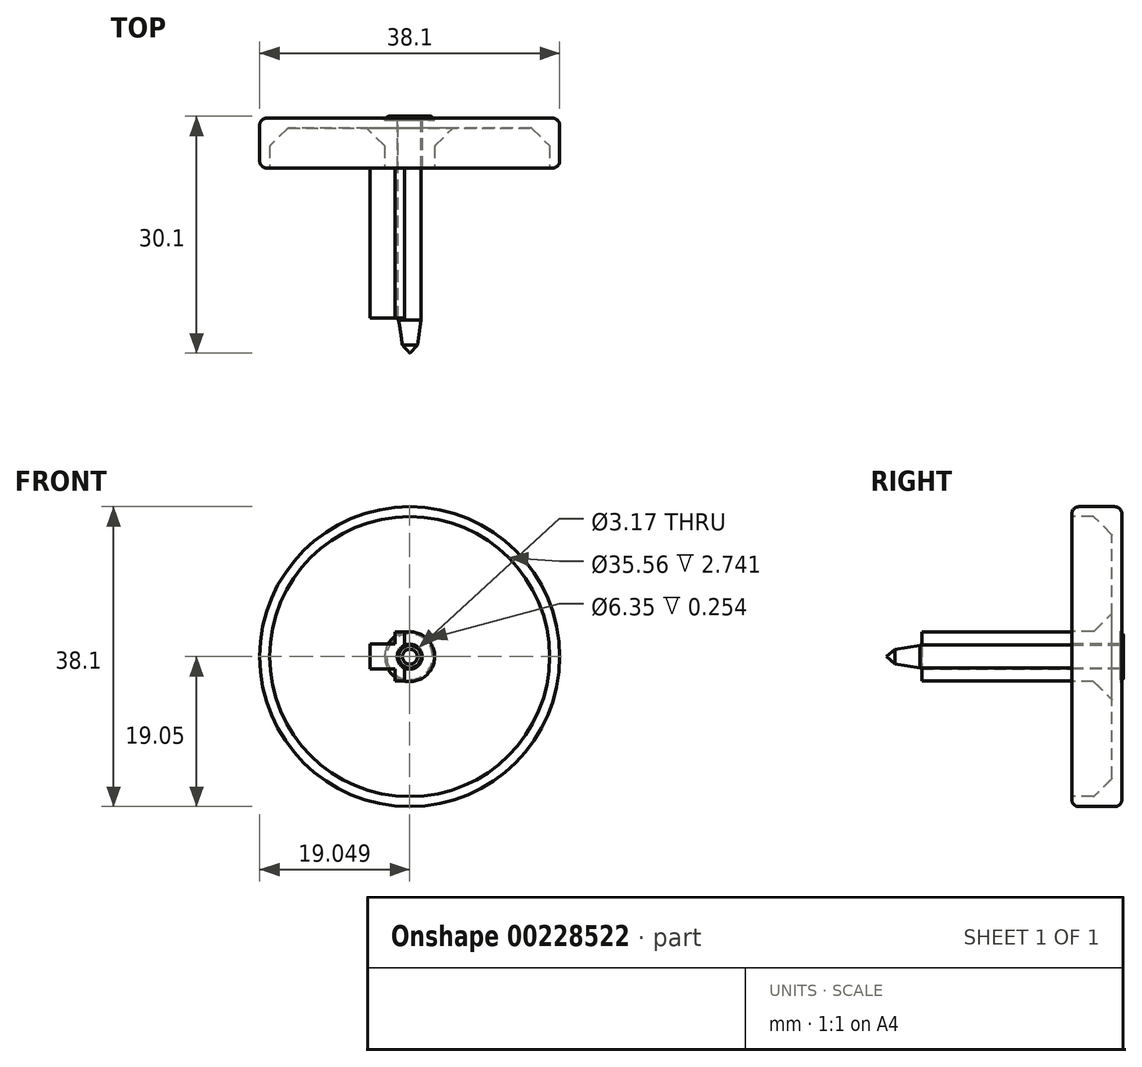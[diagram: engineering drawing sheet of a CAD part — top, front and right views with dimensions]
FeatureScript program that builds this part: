
annotation { "Feature Type Name" : "Feature", "Feature Type Description" : "" }
export const myFeature = defineFeature(function(context is Context, id is Id, definition is map)
    precondition{}
    {
        {
            var Q0;
            Q0=qCreatedBy(makeId("Front.planeOp"),FACE);
            var sketch = newSketch(context, id + "F0", { "sketchPlane" : qUnion([Q0])});
            skCircle(sketch, "E0", {"center": v(0.63, 0) * mm, "radius": 19.05 * mm});
            skSolve(sketch);
        }
        {
            var Q0;
            Q0=makeQuery(id+"F0.imprint","IMPRINT",FACE,{"disambiguationData":[TD([[makeQuery(id+"F0.imprint","IMPRINT",EDGE,{"derivedFrom":sQuery(id+"F0.wireOp",EDGE,"E0")}),1.0]])]});
            extrude(context, id + "F1", {"entities" : qUnion([Q0]), "depth" : 6.35 * mm});
        }
        {
            var Q0;
            Q0=makeQuery(id+"F1.opExtrude","CAP_FACE",FACE,{"disambiguationData":[OSD([sQuery(id+"F0.wireOp",EDGE,"E0")])],"isStart":false});
            var sketch = newSketch(context, id + "F2", { "sketchPlane" : qUnion([Q0])});
            skCircle(sketch, "E1", {"center": v(0.63, 0) * mm, "radius": 17.78 * mm});
            skCircle(sketch, "E2", {"center": v(0.63, 0) * mm, "radius": 3.18 * mm});
            skSolve(sketch);
        }
        {
            var Q0;
            Q0=makeQuery(id+"F2.imprint","IMPRINT",FACE,{"disambiguationData":[TD([[makeQuery(id+"F2.imprint","IMPRINT",EDGE,{"derivedFrom":sQuery(id+"F2.wireOp",EDGE,"E1")}),1.0]])]});
            extrude(context, id + "F3", {"entities" : qUnion([Q0]), "operationType" : NewBodyOperationType.REMOVE, "oppositeDirection" : true, "depth" : 5.08 * mm});
        }
        {
            var Q0;
            Q0=makeQuery(id+"F3.boolean.opBoolean","SPLIT",FACE,{"disambiguationData":[TD([makeQuery(id+"F3.opExtrude","SWEPT_FACE",FACE,{"disambiguationData":[OSD([sQuery(id+"F2.wireOp",EDGE,"E2")])]})])],"derivedFrom":makeQuery(id+"F1.opExtrude","CAP_FACE",FACE,{"disambiguationData":[OSD([sQuery(id+"F0.wireOp",EDGE,"E0")])],"isStart":false})});
            var sketch = newSketch(context, id + "F4", { "sketchPlane" : qUnion([Q0])});
            skCircle(sketch, "E3", {"center": v(0.63, 0) * mm, "radius": 1.59 * mm});
            skSolve(sketch);
        }
        {
            var Q0;
            Q0=qSketchRegion(id+"F4",true);
            var Q1;
            Q1=makeQuery(id+"F1.opExtrude","CAP_FACE",FACE,{"disambiguationData":[OSD([sQuery(id+"F0.wireOp",EDGE,"E0")])],"isStart":true});
            extrude(context, id + "F5", {"entities" : qUnion([Q0]), "operationType" : NewBodyOperationType.REMOVE, "endBound" : BoundingType.UP_TO_SURFACE, "oppositeDirection" : true, "endBoundEntityFace" : qUnion([Q1]), "depth" : 25.4 * mm});
        }
        {
            var Q0;
            Q0=makeQuery(id+"F1.opExtrude","CAP_FACE",FACE,{"disambiguationData":[OSD([sQuery(id+"F0.wireOp",EDGE,"E0")])],"isStart":true});
            var sketch = newSketch(context, id + "F6", { "sketchPlane" : qUnion([Q0])});
            skCircle(sketch, "E4", {"center": v(-0.63, 0) * mm, "radius": 3.18 * mm});
            skSolve(sketch);
        }
        {
            var Q0;
            Q0=qSketchRegion(id+"F6",true);
            extrude(context, id + "F7", {"entities" : qUnion([Q0]), "operationType" : NewBodyOperationType.REMOVE, "oppositeDirection" : true, "depth" : 0.25 * mm});
        }
        {
            var Q0;
            Q0=makeQuery(id+"F7.boolean.opBoolean","COPY",FACE,{"derivedFrom":makeQuery(id+"F7.opExtrude","CAP_FACE",FACE,{"disambiguationData":[OSD([sQuery(id+"F6.wireOp",EDGE,"E4")])],"isStart":false})});
            var sketch = newSketch(context, id + "F8", { "sketchPlane" : qUnion([Q0])});
            skCircle(sketch, "E5", {"center": v(-0.63, 0) * mm, "radius": 1.46 * mm});
            skSolve(sketch);
        }
        {
            var Q0;
            Q0=qSketchRegion(id+"F8",true);
            extrude(context, id + "F9", {"entities" : qUnion([Q0]), "oppositeDirection" : true, "depth" : 25.4 * mm});
        }
        {
            var Q0;
            Q0=qCreatedBy(makeId("Top.planeOp"),FACE);
            var sketch = newSketch(context, id + "F10", { "sketchPlane" : qUnion([Q0])});
            skLineSegment(sketch, "E6", {"start": v(0.66, -25.65) * mm, "end": v(0.66, -29.87) * mm});
            skLineSegment(sketch, "E7", {"start": v(0.66, -29.87) * mm, "end": v(1.6, -28.83) * mm});
            skLineSegment(sketch, "E8", {"start": v(1.6, -28.83) * mm, "end": v(2.09, -25.65) * mm});
            skLineSegment(sketch, "E9", {"start": v(2.09, -25.65) * mm, "end": v(0.66, -25.65) * mm});
            skSolve(sketch);
        }
        {
            var Q0;
            Q0=makeQuery(id+"F10.imprint","IMPRINT",FACE,{"disambiguationData":[TD([[makeQuery(id+"F10.imprint","IMPRINT",EDGE,{"derivedFrom":sQuery(id+"F10.wireOp",EDGE,"E6")}),1.0]])]});
            var Q1;
            Q1=sQuery(id+"F10.wireOp",EDGE,"E6");
            revolve(context, id + "F11", {"operationType" : NewBodyOperationType.ADD, "entities" : qUnion([Q0]), "axis" : qUnion([Q1]), "revolveType" : RevolveType.FULL});
        }
        {
            var Q0;
            Q0=makeQuery(id+"F9.opExtrude","CAP_FACE",FACE,{"disambiguationData":[OSD([sQuery(id+"F8.wireOp",EDGE,"E5")])],"isStart":true});
            var sketch = newSketch(context, id + "F12", { "sketchPlane" : qUnion([Q0])});
            skCircle(sketch, "E10", {"center": v(-0.63, 0) * mm, "radius": 2.92 * mm});
            skSolve(sketch);
        }
        {
            var Q0;
            Q0=qSketchRegion(id+"F12",true);
            extrude(context, id + "F13", {"entities" : qUnion([Q0]), "depth" : 0.48 * mm});
        }
        {
            var Q0;
            Q0=makeQuery(id+"F13.opExtrude","CAP_EDGE",EDGE,{"disambiguationData":[OSD([sQuery(id+"F12.wireOp",EDGE,"E10")])],"isStart":false});
            var Q1;
            Q1=makeQuery(id+"F7.boolean.opBoolean","COPY",EDGE,{"derivedFrom":makeQuery(id+"F7.opExtrude","CAP_EDGE",EDGE,{"disambiguationData":[OSD([sQuery(id+"F6.wireOp",EDGE,"E4")])],"isStart":true})});
            fillet(context, id + "F14", {"entities" : qUnion([Q0, Q1]), "radius" : 0.25 * mm, "tangentPropagation" : true, "allowEdgeOverflow" : false});
        }
        {
            var Q0;
            Q0=makeQuery(id+"F1.opExtrude","CAP_EDGE",EDGE,{"disambiguationData":[OSD([sQuery(id+"F0.wireOp",EDGE,"E0")])],"isStart":true});
            var Q1;
            Q1=makeQuery(id+"F1.opExtrude","CAP_EDGE",EDGE,{"disambiguationData":[OSD([sQuery(id+"F0.wireOp",EDGE,"E0")])],"isStart":false});
            fillet(context, id + "F15", {"entities" : qUnion([Q0, Q1]), "radius" : 0.89 * mm, "tangentPropagation" : true, "allowEdgeOverflow" : false});
        }
        {
            var Q0;
            Q0=makeQuery(id+"F3.boolean.opBoolean","COPY",FACE,{"derivedFrom":makeQuery(id+"F3.opExtrude","CAP_FACE",FACE,{"disambiguationData":[OSD([sQuery(id+"F2.wireOp",EDGE,"E1"),sQuery(id+"F2.wireOp",EDGE,"E2")])],"isStart":false})});
            chamfer(context, id + "F16", {"entities" : qUnion([Q0]), "width" : 2.3 * mm, "tangentPropagation" : true});
        }
        {
            var Q0;
            {var subQ0=sQuery(id+"F2.wireOp",EDGE,"E1");Q0=makeQuery(id+"F16.opChamfer","BLEND_EDGE",EDGE,{"blendedFrom":[makeQuery(id+"F3.boolean.opBoolean","COPY",EDGE,{"derivedFrom":makeQuery(id+"F3.opExtrude","CAP_EDGE",EDGE,{"disambiguationData":[OSD([subQ0])],"isStart":false})}),makeQuery(id+"F3.boolean.opBoolean","COPY",FACE,{"derivedFrom":makeQuery(id+"F3.opExtrude","CAP_FACE",FACE,{"disambiguationData":[OSD([subQ0,sQuery(id+"F2.wireOp",EDGE,"E2")])],"isStart":false})})],"blendedInto":[makeQuery(id+"F3.boolean.opBoolean","COPY",FACE,{"derivedFrom":makeQuery(id+"F3.opExtrude","CAP_FACE",FACE,{"disambiguationData":[OSD([subQ0,sQuery(id+"F2.wireOp",EDGE,"E2")])],"isStart":false})})]});}
            var Q1;
            {var subQ0=sQuery(id+"F2.wireOp",EDGE,"E2");Q1=makeQuery(id+"F16.opChamfer","BLEND_EDGE",EDGE,{"blendedFrom":[makeQuery(id+"F3.boolean.opBoolean","COPY",EDGE,{"derivedFrom":makeQuery(id+"F3.opExtrude","CAP_EDGE",EDGE,{"disambiguationData":[OSD([subQ0])],"isStart":false})}),makeQuery(id+"F3.boolean.opBoolean","COPY",FACE,{"derivedFrom":makeQuery(id+"F3.opExtrude","CAP_FACE",FACE,{"disambiguationData":[OSD([sQuery(id+"F2.wireOp",EDGE,"E1"),subQ0])],"isStart":false})})],"blendedInto":[makeQuery(id+"F3.boolean.opBoolean","COPY",FACE,{"derivedFrom":makeQuery(id+"F3.opExtrude","CAP_FACE",FACE,{"disambiguationData":[OSD([sQuery(id+"F2.wireOp",EDGE,"E1"),subQ0])],"isStart":false})})]});}
            var Q2;
            {var subQ0=sQuery(id+"F2.wireOp",EDGE,"E2");Q2=makeQuery(id+"F16.opChamfer","BLEND_EDGE",EDGE,{"blendedFrom":[makeQuery(id+"F3.boolean.opBoolean","COPY",EDGE,{"derivedFrom":makeQuery(id+"F3.opExtrude","CAP_EDGE",EDGE,{"disambiguationData":[OSD([subQ0])],"isStart":false})}),makeQuery(id+"F3.boolean.opBoolean","COPY",FACE,{"derivedFrom":makeQuery(id+"F3.opExtrude","SWEPT_FACE",FACE,{"disambiguationData":[OSD([subQ0])]})})],"blendedInto":[makeQuery(id+"F3.boolean.opBoolean","COPY",FACE,{"derivedFrom":makeQuery(id+"F3.opExtrude","SWEPT_FACE",FACE,{"disambiguationData":[OSD([subQ0])]})})]});}
            var Q3;
            {var subQ0=sQuery(id+"F2.wireOp",EDGE,"E1");Q3=makeQuery(id+"F16.opChamfer","BLEND_EDGE",EDGE,{"blendedFrom":[makeQuery(id+"F3.boolean.opBoolean","COPY",EDGE,{"derivedFrom":makeQuery(id+"F3.opExtrude","CAP_EDGE",EDGE,{"disambiguationData":[OSD([subQ0])],"isStart":false})}),makeQuery(id+"F3.boolean.opBoolean","COPY",FACE,{"derivedFrom":makeQuery(id+"F3.opExtrude","SWEPT_FACE",FACE,{"disambiguationData":[OSD([subQ0])]})})],"blendedInto":[makeQuery(id+"F3.boolean.opBoolean","COPY",FACE,{"derivedFrom":makeQuery(id+"F3.opExtrude","SWEPT_FACE",FACE,{"disambiguationData":[OSD([subQ0])]})})]});}
            fillet(context, id + "F17", {"entities" : qUnion([Q0, Q1, Q2, Q3]), "radius" : 0.13 * mm, "tangentPropagation" : true, "allowEdgeOverflow" : false});
        }
        {
            var Q0;
            Q0=makeQuery(id+"F3.boolean.opBoolean","SPLIT",FACE,{"disambiguationData":[TD([makeQuery(id+"F3.opExtrude","SWEPT_FACE",FACE,{"disambiguationData":[OSD([sQuery(id+"F2.wireOp",EDGE,"E2")])]})])],"derivedFrom":makeQuery(id+"F1.opExtrude","CAP_FACE",FACE,{"disambiguationData":[OSD([sQuery(id+"F0.wireOp",EDGE,"E0")])],"isStart":false})});
            var sketch = newSketch(context, id + "F18", { "sketchPlane" : qUnion([Q0])});
            skLineSegment(sketch, "E11.bottom", {"start": v(0, 3.11) * mm, "end": v(-1.22, 3.11) * mm});
            skLineSegment(sketch, "E11.top", {"start": v(0, -3.11) * mm, "end": v(-1.22, -3.11) * mm});
            skLineSegment(sketch, "E11.left", {"start": v(0, 3.11) * mm, "end": v(0, 1.46) * mm});
            skArc(sketch, "E12.0", {"start": v(0, 1.46) * mm, "mid": v(-0.96, 0) * mm, "end": v(0, -1.46) * mm});
            skLineSegment(sketch, "E13.trimOffspring", {"start": v(0, -1.46) * mm, "end": v(0, -3.11) * mm});
            skLineSegment(sketch, "E14", {"start": v(-1.22, -3.11) * mm, "end": v(-1.22, -1.59) * mm});
            skLineSegment(sketch, "E15", {"start": v(-1.22, -1.59) * mm, "end": v(-4.4, -1.59) * mm});
            skLineSegment(sketch, "E16", {"start": v(-4.4, -1.59) * mm, "end": v(-4.4, 1.59) * mm});
            skLineSegment(sketch, "E17", {"start": v(-4.4, 1.59) * mm, "end": v(-1.22, 1.59) * mm});
            skLineSegment(sketch, "E18", {"start": v(-1.22, 1.59) * mm, "end": v(-1.22, 3.11) * mm});
            skSolve(sketch);
        }
        {
            var Q0;
            Q0=qSketchRegion(id+"F18",true);
            extrude(context, id + "F19", {"entities" : qUnion([Q0]), "depth" : 19.05 * mm});
        }
    });
